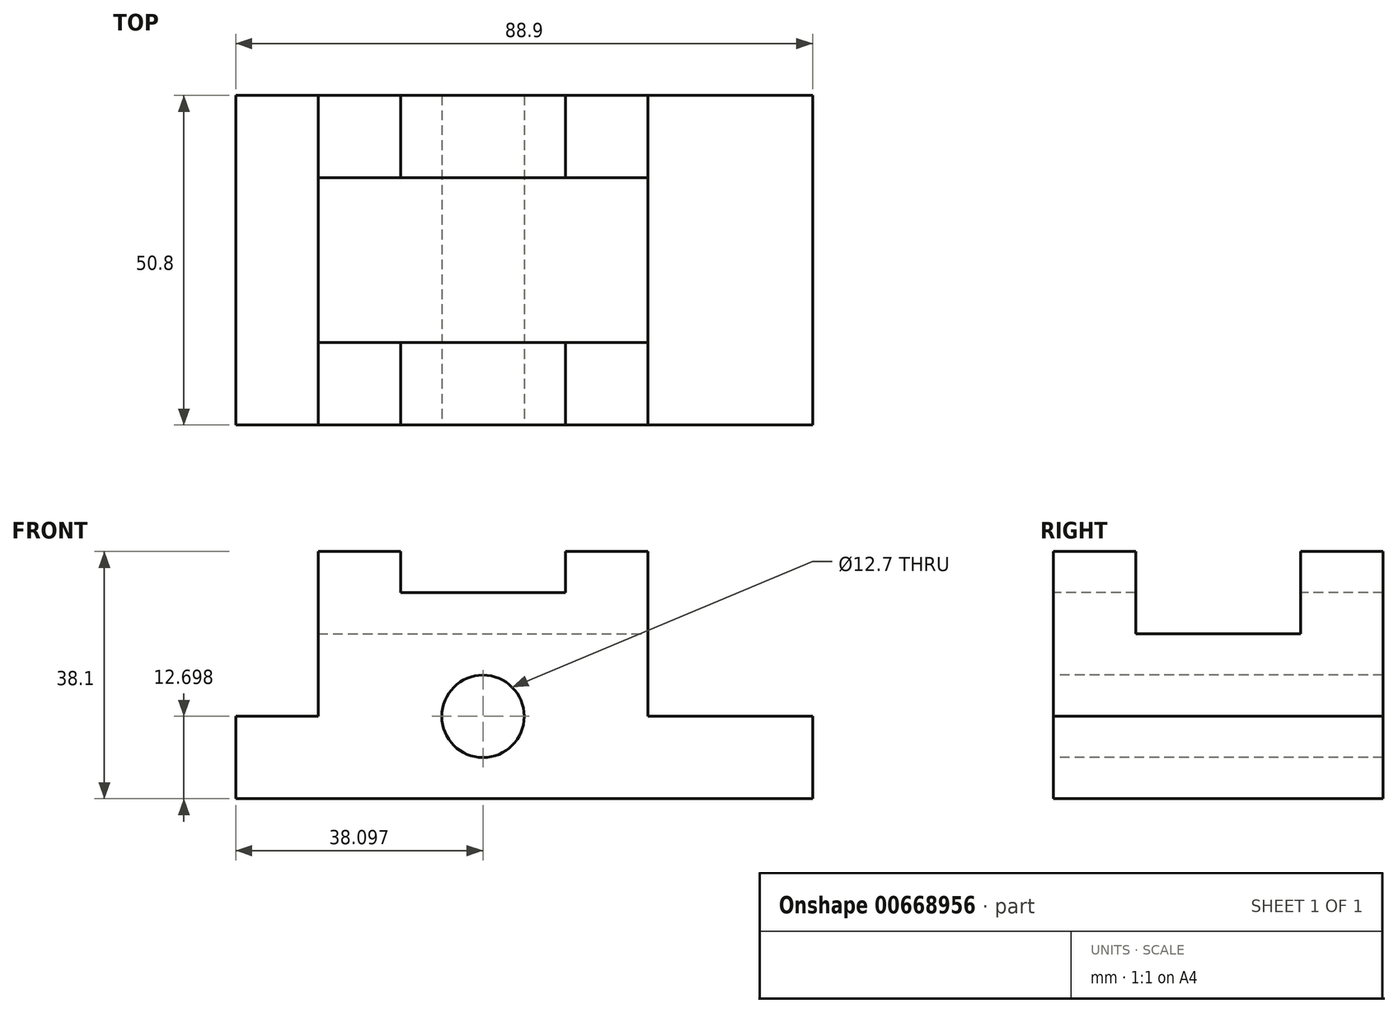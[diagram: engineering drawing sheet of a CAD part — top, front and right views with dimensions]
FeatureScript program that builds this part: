
annotation { "Feature Type Name" : "Feature", "Feature Type Description" : "" }
export const myFeature = defineFeature(function(context is Context, id is Id, definition is map)
    precondition{}
    {
        {
            var Q0;
            Q0=qCreatedBy(makeId("Front.planeOp"),FACE);
            var sketch = newSketch(context, id + "F0", { "sketchPlane" : qUnion([Q0])});
            skLineSegment(sketch, "E0.bottom", {"start": v(24.15, -10.5) * mm, "end": v(-64.75, -10.5) * mm});
            skLineSegment(sketch, "E0.top", {"start": v(24.15, 27.6) * mm, "end": v(-64.75, 27.6) * mm});
            skLineSegment(sketch, "E0.left", {"start": v(24.15, -10.5) * mm, "end": v(24.15, 27.6) * mm});
            skLineSegment(sketch, "E0.right", {"start": v(-64.75, -10.5) * mm, "end": v(-64.75, 27.6) * mm});
            skPoint(sketch, "E0.middle", {"position": v(-20.3, 8.55) * mm});
            skSolve(sketch);
        }
        {
            var Q0;
            Q0 = qSketchRegion(id + "F0", true);
            extrude(context, id + "F1", {"entities" : qUnion([Q0]), "depth" : 50.8 * mm, "offsetDistance" : 25.4 * mm});
        }
        {
            var Q0;
            Q0=makeQuery(id+"F1.opExtrude","CAP_FACE",FACE,{"disambiguationData":[OSD([sQuery(id+"F0.wireOp",EDGE,"E0.bottom"),sQuery(id+"F0.wireOp",EDGE,"E0.top"),sQuery(id+"F0.wireOp",EDGE,"E0.left"),sQuery(id+"F0.wireOp",EDGE,"E0.right")])],"isStart":false});
            var sketch = newSketch(context, id + "F2", { "sketchPlane" : qUnion([Q0])});
            skLineSegment(sketch, "E1.bottom", {"start": v(-39.35, 27.6) * mm, "end": v(-13.95, 27.6) * mm});
            skLineSegment(sketch, "E1.top", {"start": v(-39.35, 21.25) * mm, "end": v(-13.95, 21.25) * mm});
            skLineSegment(sketch, "E1.left", {"start": v(-39.35, 27.6) * mm, "end": v(-39.35, 21.25) * mm});
            skLineSegment(sketch, "E1.right", {"start": v(-13.95, 27.6) * mm, "end": v(-13.95, 21.25) * mm});
            skSolve(sketch);
        }
        {
            var Q0;
            Q0=makeQuery(id+"F2.imprint","IMPRINT",FACE,{"disambiguationData":[TD([[makeQuery(id+"F2.imprint","IMPRINT",EDGE,{"derivedFrom":sQuery(id+"F2.wireOp",EDGE,"E1.bottom")}),1.0]])]});
            extrude(context, id + "F3", {"entities" : qUnion([Q0]), "operationType" : NewBodyOperationType.REMOVE, "endBound" : BoundingType.THROUGH_ALL, "oppositeDirection" : true, "depth" : 25.4 * mm, "offsetDistance" : 25.4 * mm});
        }
        {
            var Q0;
            Q0=makeQuery(id+"F1.opExtrude","CAP_FACE",FACE,{"disambiguationData":[OSD([sQuery(id+"F0.wireOp",EDGE,"E0.bottom"),sQuery(id+"F0.wireOp",EDGE,"E0.top"),sQuery(id+"F0.wireOp",EDGE,"E0.left"),sQuery(id+"F0.wireOp",EDGE,"E0.right")])],"isStart":false});
            var sketch = newSketch(context, id + "F4", { "sketchPlane" : qUnion([Q0])});
            skLineSegment(sketch, "E2.bottom", {"start": v(-64.75, 27.6) * mm, "end": v(-52.05, 27.6) * mm});
            skLineSegment(sketch, "E2.top", {"start": v(-64.75, 2.2) * mm, "end": v(-52.05, 2.2) * mm});
            skLineSegment(sketch, "E2.left", {"start": v(-64.75, 27.6) * mm, "end": v(-64.75, 2.2) * mm});
            skLineSegment(sketch, "E2.right", {"start": v(-52.05, 27.6) * mm, "end": v(-52.05, 2.2) * mm});
            skSolve(sketch);
        }
        {
            var Q0;
            Q0=makeQuery(id+"F4.imprint","IMPRINT",FACE,{"disambiguationData":[TD([[makeQuery(id+"F4.imprint","IMPRINT",EDGE,{"derivedFrom":sQuery(id+"F4.wireOp",EDGE,"E2.bottom")}),1.0]])]});
            extrude(context, id + "F5", {"entities" : qUnion([Q0]), "operationType" : NewBodyOperationType.REMOVE, "endBound" : BoundingType.THROUGH_ALL, "oppositeDirection" : true, "depth" : 25.4 * mm, "offsetDistance" : 25.4 * mm});
        }
        {
            var Q0;
            Q0=makeQuery(id+"F1.opExtrude","CAP_FACE",FACE,{"disambiguationData":[OSD([sQuery(id+"F0.wireOp",EDGE,"E0.bottom"),sQuery(id+"F0.wireOp",EDGE,"E0.top"),sQuery(id+"F0.wireOp",EDGE,"E0.left"),sQuery(id+"F0.wireOp",EDGE,"E0.right")])],"isStart":false});
            var sketch = newSketch(context, id + "F6", { "sketchPlane" : qUnion([Q0])});
            skLineSegment(sketch, "E3.bottom", {"start": v(24.15, 27.6) * mm, "end": v(-1.25, 27.6) * mm});
            skLineSegment(sketch, "E3.top", {"start": v(24.15, 2.2) * mm, "end": v(-1.25, 2.2) * mm});
            skLineSegment(sketch, "E3.left", {"start": v(24.15, 27.6) * mm, "end": v(24.15, 2.2) * mm});
            skLineSegment(sketch, "E3.right", {"start": v(-1.25, 27.6) * mm, "end": v(-1.25, 2.2) * mm});
            skSolve(sketch);
        }
        {
            var Q0;
            Q0 = qSketchRegion(id + "F6", true);
            extrude(context, id + "F7", {"entities" : qUnion([Q0]), "operationType" : NewBodyOperationType.REMOVE, "endBound" : BoundingType.THROUGH_ALL, "oppositeDirection" : true, "depth" : 25.4 * mm, "offsetDistance" : 25.4 * mm});
        }
        {
            var Q0;
            Q0=makeQuery(id+"F7.boolean.opBoolean","COPY",FACE,{"derivedFrom":makeQuery(id+"F7.opExtrude","SWEPT_FACE",FACE,{"disambiguationData":[OSD([sQuery(id+"F6.wireOp",EDGE,"E3.right")])]})});
            var sketch = newSketch(context, id + "F8", { "sketchPlane" : qUnion([Q0])});
            skLineSegment(sketch, "E4.bottom", {"start": v(-38.1, 27.6) * mm, "end": v(-12.7, 27.6) * mm});
            skLineSegment(sketch, "E4.top", {"start": v(-38.1, 14.9) * mm, "end": v(-12.7, 14.9) * mm});
            skLineSegment(sketch, "E4.left", {"start": v(-38.1, 27.6) * mm, "end": v(-38.1, 14.9) * mm});
            skLineSegment(sketch, "E4.right", {"start": v(-12.7, 27.6) * mm, "end": v(-12.7, 14.9) * mm});
            skSolve(sketch);
        }
        {
            var Q0;
            Q0=makeQuery(id+"F8.imprint","IMPRINT",FACE,{"disambiguationData":[TD([[makeQuery(id+"F8.imprint","IMPRINT",EDGE,{"derivedFrom":sQuery(id+"F8.wireOp",EDGE,"E4.bottom")}),1.0]])]});
            extrude(context, id + "F9", {"entities" : qUnion([Q0]), "operationType" : NewBodyOperationType.REMOVE, "endBound" : BoundingType.THROUGH_ALL, "oppositeDirection" : true, "depth" : 25.4 * mm, "offsetDistance" : 25.4 * mm});
        }
        {
            var Q0;
            Q0=makeQuery(id+"F1.opExtrude","CAP_FACE",FACE,{"disambiguationData":[OSD([sQuery(id+"F0.wireOp",EDGE,"E0.bottom"),sQuery(id+"F0.wireOp",EDGE,"E0.top"),sQuery(id+"F0.wireOp",EDGE,"E0.left"),sQuery(id+"F0.wireOp",EDGE,"E0.right")])],"isStart":false});
            var sketch = newSketch(context, id + "F10", { "sketchPlane" : qUnion([Q0])});
            skCircle(sketch, "E5", {"center": v(-26.65, 2.2) * mm, "radius": 6.35 * mm});
            skSolve(sketch);
        }
        {
            var Q0;
            Q0=makeQuery(id+"F10.imprint","IMPRINT",FACE,{"disambiguationData":[TD([[makeQuery(id+"F10.imprint","IMPRINT",EDGE,{"derivedFrom":sQuery(id+"F10.wireOp",EDGE,"E5")}),1.0]])]});
            extrude(context, id + "F11", {"entities" : qUnion([Q0]), "operationType" : NewBodyOperationType.REMOVE, "endBound" : BoundingType.THROUGH_ALL, "oppositeDirection" : true, "depth" : 25.4 * mm, "offsetDistance" : 25.4 * mm});
        }
    });
